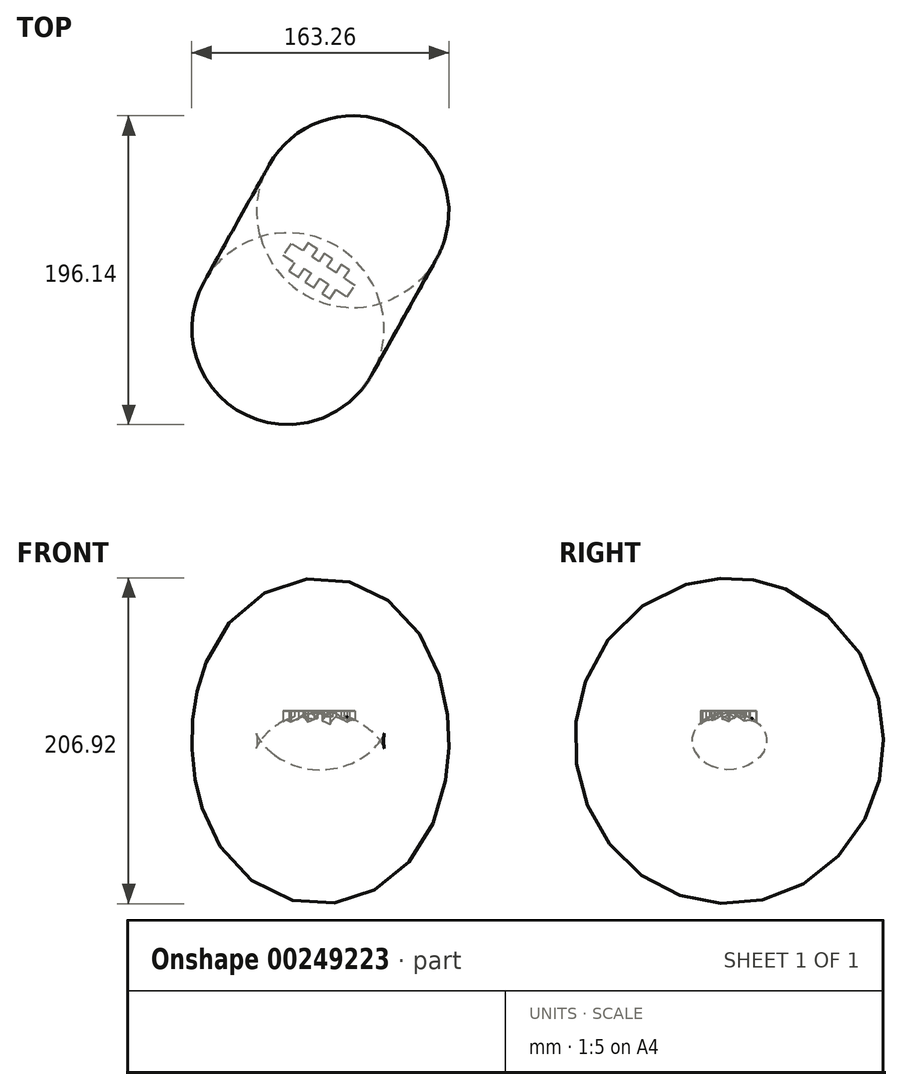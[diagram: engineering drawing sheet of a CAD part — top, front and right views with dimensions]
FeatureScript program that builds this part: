
annotation { "Feature Type Name" : "Feature", "Feature Type Description" : "" }
export const myFeature = defineFeature(function(context is Context, id is Id, definition is map)
    precondition{}
    {
        {
            var Q0;
            Q0=qCreatedBy(makeId("Top.planeOp"),FACE);
            var sketch = newSketch(context, id + "F0", { "sketchPlane" : qUnion([Q0])});
            skArc(sketch, "E0", {"start": v(0, -42.42) * mm, "mid": v(-29.1, -5.2) * mm, "end": v(-76.06, 0) * mm});
            skLineSegment(sketch, "E1", {"start": v(-76.06, 0) * mm, "end": v(0, -42.42) * mm});
            skSolve(sketch);
        }
        {
            var Q0;
            Q0=makeQuery(id+"F0.imprint","IMPRINT",FACE,{"disambiguationData":[TD([[makeQuery(id+"F0.imprint","IMPRINT",EDGE,{"derivedFrom":sQuery(id+"F0.wireOp",EDGE,"E0")}),1.0]])]});
            var Q1;
            Q1=sQuery(id+"F0.wireOp",EDGE,"E1");
            revolve(context, id + "F1", {"entities" : qUnion([Q0]), "axis" : qUnion([Q1]), "revolveType" : RevolveType.FULL});
        }
        {
            var Q0;
            Q0=qCreatedBy(makeId("Top.planeOp"),FACE);
            var sketch = newSketch(context, id + "F2", { "sketchPlane" : qUnion([Q0])});
            skLineSegment(sketch, "E2", {"start": v(-56.62, -4.23) * mm, "end": v(-61.54, -11.62) * mm});
            skLineSegment(sketch, "E3", {"start": v(-61.54, -11.62) * mm, "end": v(-54.46, -16.33) * mm});
            skLineSegment(sketch, "E4", {"start": v(-54.46, -16.33) * mm, "end": v(-58, -21.64) * mm});
            skPoint(sketch, "E4.endSnap0", {"position": v(-58, -13.98) * mm});
            skLineSegment(sketch, "E5", {"start": v(-58, -21.64) * mm, "end": v(-51.85, -25.75) * mm});
            skLineSegment(sketch, "E6", {"start": v(-51.85, -25.75) * mm, "end": v(-48.2, -20.27) * mm});
            skLineSegment(sketch, "E7", {"start": v(-48.2, -20.27) * mm, "end": v(-43.87, -23.16) * mm});
            skLineSegment(sketch, "E8", {"start": v(-43.87, -23.16) * mm, "end": v(-47.62, -28.78) * mm});
            skLineSegment(sketch, "E9", {"start": v(-47.62, -28.78) * mm, "end": v(-42.15, -32.43) * mm});
            skLineSegment(sketch, "E10", {"start": v(-42.15, -32.43) * mm, "end": v(-38.26, -26.59) * mm});
            skLineSegment(sketch, "E11", {"start": v(-38.26, -26.59) * mm, "end": v(-32.96, -30.12) * mm});
            skLineSegment(sketch, "E12", {"start": v(-32.96, -30.12) * mm, "end": v(-36.88, -36) * mm});
            skLineSegment(sketch, "E13", {"start": v(-36.88, -36) * mm, "end": v(-31.8, -39.38) * mm});
            skLineSegment(sketch, "E14", {"start": v(-31.8, -39.38) * mm, "end": v(-28, -33.67) * mm});
            skLineSegment(sketch, "E15", {"start": v(-28, -33.67) * mm, "end": v(-20.95, -38.37) * mm});
            skLineSegment(sketch, "E16", {"start": v(-20.95, -38.37) * mm, "end": v(-16.03, -31) * mm});
            skLineSegment(sketch, "E17", {"start": v(-16.03, -31) * mm, "end": v(-23.04, -26.32) * mm});
            skLineSegment(sketch, "E18", {"start": v(-23.04, -26.32) * mm, "end": v(-19.6, -21.16) * mm});
            skLineSegment(sketch, "E19", {"start": v(-19.6, -21.16) * mm, "end": v(-24.77, -17.71) * mm});
            skLineSegment(sketch, "E20", {"start": v(-24.77, -17.71) * mm, "end": v(-28.2, -22.87) * mm});
            skLineSegment(sketch, "E21", {"start": v(-28.2, -22.87) * mm, "end": v(-33.68, -19.22) * mm});
            skLineSegment(sketch, "E22", {"start": v(-33.68, -19.22) * mm, "end": v(-30.33, -14.2) * mm});
            skLineSegment(sketch, "E23", {"start": v(-30.33, -14.2) * mm, "end": v(-35.56, -10.7) * mm});
            skLineSegment(sketch, "E24", {"start": v(-35.56, -10.7) * mm, "end": v(-38.86, -15.65) * mm});
            skLineSegment(sketch, "E25", {"start": v(-38.86, -15.65) * mm, "end": v(-43.14, -12.8) * mm});
            skLineSegment(sketch, "E26", {"start": v(-43.14, -12.8) * mm, "end": v(-39.9, -7.93) * mm});
            skLineSegment(sketch, "E27", {"start": v(-39.9, -7.93) * mm, "end": v(-45.92, -3.91) * mm});
            skLineSegment(sketch, "E28", {"start": v(-45.92, -3.91) * mm, "end": v(-49.17, -8.77) * mm});
            skLineSegment(sketch, "E29", {"start": v(-49.17, -8.77) * mm, "end": v(-56.62, -4.23) * mm});
            skSolve(sketch);
        }
        {
            var Q0;
            Q0 = qSketchRegion(id + "F2", true);
            extrude(context, id + "F3", {"entities" : qUnion([Q0]), "operationType" : NewBodyOperationType.ADD, "depth" : 19.05 * mm});
        }
    });
